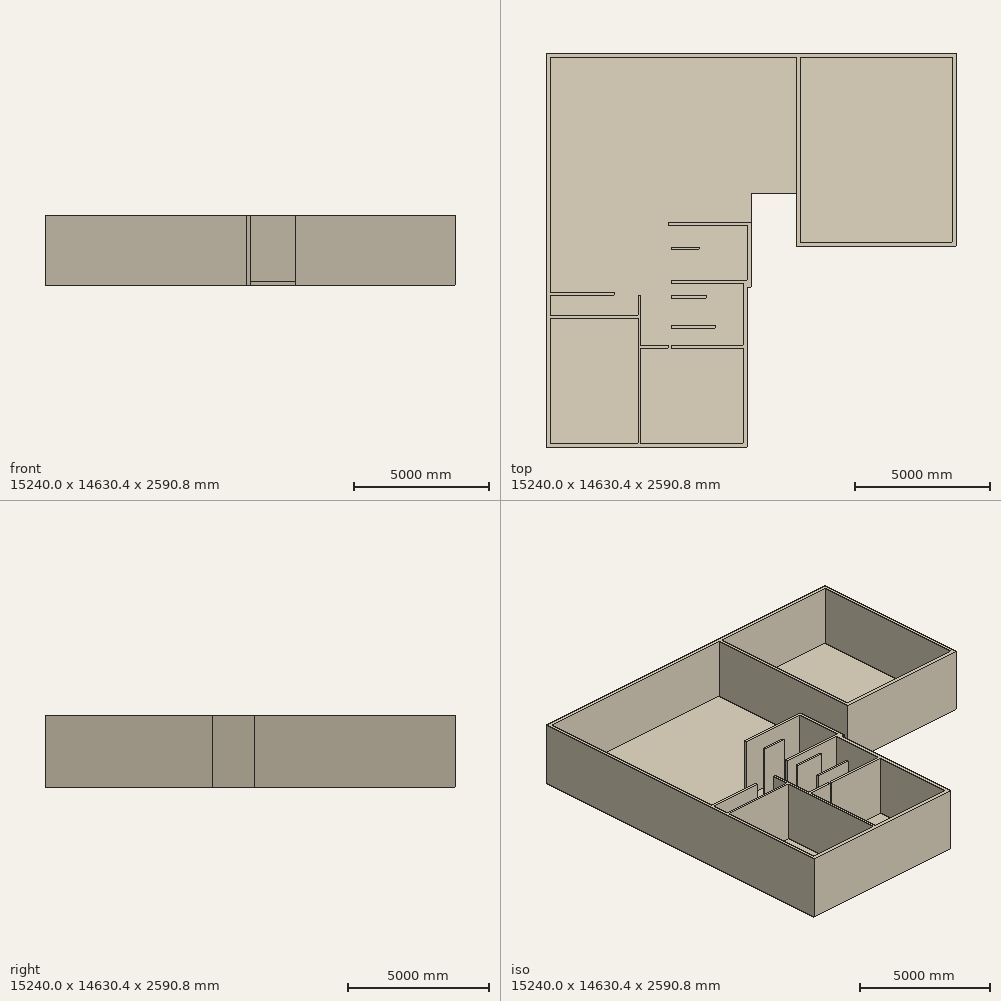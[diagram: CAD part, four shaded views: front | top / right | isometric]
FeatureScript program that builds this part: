
annotation { "Feature Type Name" : "Feature", "Feature Type Description" : "" }
export const myFeature = defineFeature(function(context is Context, id is Id, definition is map)
    precondition{}
    {
        {
            var Q0;
            Q0=qCreatedBy(makeId("Top.planeOp"),FACE);
            var sketch = newSketch(context, id + "F0", { "sketchPlane" : qUnion([Q0])});
            skLineSegment(sketch, "E0", {"start": v(0, 0) * mm, "end": v(0, -14630.4) * mm});
            skLineSegment(sketch, "E1", {"start": v(0, -14630.4) * mm, "end": v(7467.6, -14630.4) * mm});
            skLineSegment(sketch, "E2", {"start": v(7620, -8686.8) * mm, "end": v(7620, -5181.6) * mm});
            skLineSegment(sketch, "E3", {"start": v(7620, -5181.6) * mm, "end": v(9296.4, -5181.6) * mm});
            skLineSegment(sketch, "E4", {"start": v(9296.4, -5181.6) * mm, "end": v(9296.4, -7162.8) * mm});
            skLineSegment(sketch, "E5", {"start": v(9296.4, -7162.8) * mm, "end": v(15240, -7162.8) * mm});
            skLineSegment(sketch, "E6", {"start": v(15240, -7162.8) * mm, "end": v(15240, 0) * mm});
            skLineSegment(sketch, "E7", {"start": v(15240, 0) * mm, "end": v(0, 0) * mm});
            skLineSegment(sketch, "E8.0", {"start": v(15087.6, -152.4) * mm, "end": v(152.4, -152.4) * mm});
            skLineSegment(sketch, "E8.1", {"start": v(15087.6, -7010.4) * mm, "end": v(15087.6, -152.4) * mm});
            skLineSegment(sketch, "E8.2", {"start": v(9448.8, -7010.4) * mm, "end": v(15087.6, -7010.4) * mm});
            skLineSegment(sketch, "E8.3", {"start": v(9448.8, -5029.2) * mm, "end": v(9448.8, -7010.4) * mm});
            skLineSegment(sketch, "E8.4", {"start": v(7467.6, -5029.2) * mm, "end": v(9448.8, -5029.2) * mm});
            skLineSegment(sketch, "E8.5", {"start": v(152.4, -152.4) * mm, "end": v(152.4, -14478) * mm});
            skLineSegment(sketch, "E8.6", {"start": v(7467.6, -8534.4) * mm, "end": v(7467.6, -5029.2) * mm});
            skLineSegment(sketch, "E8.7", {"start": v(152.4, -14478) * mm, "end": v(7315.2, -14478) * mm});
            skLineSegment(sketch, "E9", {"start": v(7315.2, -14478) * mm, "end": v(7315.2, -8534.4) * mm});
            skLineSegment(sketch, "E10", {"start": v(7315.2, -8534.4) * mm, "end": v(7467.6, -8534.4) * mm});
            skLineSegment(sketch, "E11.0", {"start": v(7467.6, -8686.8) * mm, "end": v(7620, -8686.8) * mm});
            skLineSegment(sketch, "E11.1", {"start": v(7467.6, -14630.4) * mm, "end": v(7467.6, -8686.8) * mm});
            skSolve(sketch);
        }
        {
            var Q0;
            Q0=makeQuery(id+"F0.imprint","IMPRINT",FACE,{"disambiguationData":[TD([[makeQuery(id+"F0.imprint","IMPRINT",EDGE,{"derivedFrom":sQuery(id+"F0.wireOp",EDGE,"E0")}),1.0]])]});
            var Q1;
            Q1=makeQuery(id+"F0.imprint","IMPRINT",FACE,{"disambiguationData":[TD([[makeQuery(id+"F0.imprint","IMPRINT",EDGE,{"derivedFrom":sQuery(id+"F0.wireOp",EDGE,"E8.0")}),1.0]])]});
            extrude(context, id + "F1", {"entities" : qUnion([Q0, Q1]), "oppositeDirection" : true, "depth" : 152.4 * mm});
        }
        {
            var Q0;
            Q0=makeQuery(id+"F0.imprint","IMPRINT",FACE,{"disambiguationData":[TD([[makeQuery(id+"F0.imprint","IMPRINT",EDGE,{"derivedFrom":sQuery(id+"F0.wireOp",EDGE,"E0")}),1.0]])]});
            extrude(context, id + "F2", {"entities" : qUnion([Q0]), "depth" : 2438.4 * mm});
        }
        {
            var Q0;
            Q0=qCreatedBy(makeId("Top.planeOp"),FACE);
            var sketch = newSketch(context, id + "F3", { "sketchPlane" : qUnion([Q0])});
            skLineSegment(sketch, "E12.bottom", {"start": v(9448.8, -5029.2) * mm, "end": v(9296.4, -5029.2) * mm});
            skLineSegment(sketch, "E12.top", {"start": v(9448.8, -152.4) * mm, "end": v(9296.4, -152.4) * mm});
            skLineSegment(sketch, "E12.left", {"start": v(9448.8, -5029.2) * mm, "end": v(9448.8, -152.4) * mm});
            skLineSegment(sketch, "E12.right", {"start": v(9296.4, -5029.2) * mm, "end": v(9296.4, -152.4) * mm});
            skLineSegment(sketch, "E13.bottom", {"start": v(7467.6, -5029.2) * mm, "end": v(4546.6, -5029.2) * mm});
            skLineSegment(sketch, "E13.top", {"start": v(7467.6, -5130.8) * mm, "end": v(4546.6, -5130.8) * mm});
            skLineSegment(sketch, "E13.left", {"start": v(7467.6, -5029.2) * mm, "end": v(7467.6, -5130.8) * mm});
            skLineSegment(sketch, "E13.right", {"start": v(4546.6, -5029.2) * mm, "end": v(4546.6, -5130.8) * mm});
            skLineSegment(sketch, "E14.bottom", {"start": v(6096, -5029.2) * mm, "end": v(6197.6, -5029.2) * mm});
            skLineSegment(sketch, "E14.top", {"start": v(6096, -1625.6) * mm, "end": v(6197.6, -1625.6) * mm});
            skLineSegment(sketch, "E14.left", {"start": v(6096, -5029.2) * mm, "end": v(6096, -1625.6) * mm});
            skLineSegment(sketch, "E14.right", {"start": v(6197.6, -5029.2) * mm, "end": v(6197.6, -1625.6) * mm});
            skLineSegment(sketch, "E15.bottom", {"start": v(4546.6, -5029.2) * mm, "end": v(4648.2, -5029.2) * mm});
            skLineSegment(sketch, "E15.top", {"start": v(4546.6, -4191) * mm, "end": v(4648.2, -4191) * mm});
            skLineSegment(sketch, "E15.left", {"start": v(4546.6, -5029.2) * mm, "end": v(4546.6, -4191) * mm});
            skLineSegment(sketch, "E15.right", {"start": v(4648.2, -5029.2) * mm, "end": v(4648.2, -4191) * mm});
            skLineSegment(sketch, "E16.bottom", {"start": v(4648.2, -4191) * mm, "end": v(6096, -4191) * mm});
            skLineSegment(sketch, "E16.top", {"start": v(4648.2, -4292.6) * mm, "end": v(6096, -4292.6) * mm});
            skLineSegment(sketch, "E16.left", {"start": v(4648.2, -4191) * mm, "end": v(4648.2, -4292.6) * mm});
            skLineSegment(sketch, "E16.right", {"start": v(6096, -4191) * mm, "end": v(6096, -4292.6) * mm});
            skLineSegment(sketch, "E17.bottom", {"start": v(152.4, -4191) * mm, "end": v(3505.2, -4191) * mm});
            skLineSegment(sketch, "E17.top", {"start": v(152.4, -4292.6) * mm, "end": v(3505.2, -4292.6) * mm});
            skLineSegment(sketch, "E17.left", {"start": v(152.4, -4191) * mm, "end": v(152.4, -4292.6) * mm});
            skLineSegment(sketch, "E17.right", {"start": v(3505.2, -4191) * mm, "end": v(3505.2, -4292.6) * mm});
            skLineSegment(sketch, "E18.bottom", {"start": v(3505.2, -4292.6) * mm, "end": v(3403.6, -4292.6) * mm});
            skLineSegment(sketch, "E18.top", {"start": v(3505.2, -8991.6) * mm, "end": v(3403.6, -8991.6) * mm});
            skLineSegment(sketch, "E18.left", {"start": v(3505.2, -4292.6) * mm, "end": v(3505.2, -8991.6) * mm});
            skLineSegment(sketch, "E18.right", {"start": v(3403.6, -4292.6) * mm, "end": v(3403.6, -8991.6) * mm});
            skLineSegment(sketch, "E19.bottom", {"start": v(2540, -8991.6) * mm, "end": v(152.4, -8991.6) * mm});
            skLineSegment(sketch, "E19.top", {"start": v(2540, -8890) * mm, "end": v(152.4, -8890) * mm});
            skLineSegment(sketch, "E19.left", {"start": v(3403.6, -8991.6) * mm, "end": v(3403.6, -8890) * mm});
            skLineSegment(sketch, "E19.right", {"start": v(152.4, -8991.6) * mm, "end": v(152.4, -8890) * mm});
            skLineSegment(sketch, "E20.bottom", {"start": v(3403.6, -8051.8) * mm, "end": v(152.4, -8051.8) * mm});
            skLineSegment(sketch, "E20.top", {"start": v(3403.6, -8153.4) * mm, "end": v(152.4, -8153.4) * mm});
            skLineSegment(sketch, "E20.left", {"start": v(3403.6, -8051.8) * mm, "end": v(3403.6, -8153.4) * mm});
            skLineSegment(sketch, "E20.right", {"start": v(152.4, -8051.8) * mm, "end": v(152.4, -8153.4) * mm});
            skLineSegment(sketch, "E21.bottom", {"start": v(7467.6, -6375.4) * mm, "end": v(4546.6, -6375.4) * mm});
            skLineSegment(sketch, "E21.top", {"start": v(7467.6, -6273.8) * mm, "end": v(4546.6, -6273.8) * mm});
            skLineSegment(sketch, "E21.left", {"start": v(7467.6, -6375.4) * mm, "end": v(7467.6, -6273.8) * mm});
            skLineSegment(sketch, "E21.right", {"start": v(4546.6, -6375.4) * mm, "end": v(4546.6, -6273.8) * mm});
            skLineSegment(sketch, "E22.bottom", {"start": v(4546.6, -6375.4) * mm, "end": v(4648.2, -6375.4) * mm});
            skLineSegment(sketch, "E22.top", {"start": v(4546.6, -10947.4) * mm, "end": v(4648.2, -10947.4) * mm});
            skLineSegment(sketch, "E22.left", {"start": v(4546.6, -6375.4) * mm, "end": v(4546.6, -10947.4) * mm});
            skLineSegment(sketch, "E22.right", {"start": v(4648.2, -6375.4) * mm, "end": v(4648.2, -10947.4) * mm});
            skLineSegment(sketch, "E23.bottom", {"start": v(4648.2, -8432.8) * mm, "end": v(7467.6, -8432.8) * mm});
            skLineSegment(sketch, "E23.top", {"start": v(4648.2, -8534.4) * mm, "end": v(7467.6, -8534.4) * mm});
            skLineSegment(sketch, "E23.left", {"start": v(4648.2, -8432.8) * mm, "end": v(4648.2, -8534.4) * mm});
            skLineSegment(sketch, "E23.right", {"start": v(7467.6, -8432.8) * mm, "end": v(7467.6, -8534.4) * mm});
            skLineSegment(sketch, "E24.bottom", {"start": v(4648.2, -10947.4) * mm, "end": v(7315.2, -10947.4) * mm});
            skLineSegment(sketch, "E24.top", {"start": v(4648.2, -10845.8) * mm, "end": v(7315.2, -10845.8) * mm});
            skLineSegment(sketch, "E24.left", {"start": v(4648.2, -10947.4) * mm, "end": v(4648.2, -10845.8) * mm});
            skLineSegment(sketch, "E24.right", {"start": v(7315.2, -10947.4) * mm, "end": v(7315.2, -10845.8) * mm});
            skLineSegment(sketch, "E25.top", {"start": v(3505.2, -14478) * mm, "end": v(3403.6, -14478) * mm});
            skLineSegment(sketch, "E25.left", {"start": v(3505.2, -8991.6) * mm, "end": v(3505.2, -14478) * mm});
            skLineSegment(sketch, "E25.right", {"start": v(3403.6, -8991.6) * mm, "end": v(3403.6, -14478) * mm});
            skLineSegment(sketch, "E26.bottom", {"start": v(3403.6, -9829.8) * mm, "end": v(152.4, -9829.8) * mm});
            skLineSegment(sketch, "E26.top", {"start": v(3403.6, -9728.2) * mm, "end": v(152.4, -9728.2) * mm});
            skLineSegment(sketch, "E26.left", {"start": v(3403.6, -9829.8) * mm, "end": v(3403.6, -9728.2) * mm});
            skLineSegment(sketch, "E26.right", {"start": v(152.4, -9829.8) * mm, "end": v(152.4, -9728.2) * mm});
            skLineSegment(sketch, "E27.bottom", {"start": v(4546.6, -10947.4) * mm, "end": v(3505.2, -10947.4) * mm});
            skLineSegment(sketch, "E27.top", {"start": v(4546.6, -10845.8) * mm, "end": v(3505.2, -10845.8) * mm});
            skLineSegment(sketch, "E27.left", {"start": v(4546.6, -10947.4) * mm, "end": v(4546.6, -10845.8) * mm});
            skLineSegment(sketch, "E27.right", {"start": v(3505.2, -10947.4) * mm, "end": v(3505.2, -10845.8) * mm});
            skLineSegment(sketch, "E28.bottom", {"start": v(4648.2, -10210.8) * mm, "end": v(6273.8, -10210.8) * mm});
            skLineSegment(sketch, "E28.top", {"start": v(4648.2, -10109.2) * mm, "end": v(6273.8, -10109.2) * mm});
            skLineSegment(sketch, "E28.left", {"start": v(4648.2, -10210.8) * mm, "end": v(4648.2, -10109.2) * mm});
            skLineSegment(sketch, "E28.right", {"start": v(6273.8, -10210.8) * mm, "end": v(6273.8, -10109.2) * mm});
            skLineSegment(sketch, "E29.bottom", {"start": v(6273.8, -10210.8) * mm, "end": v(6172.2, -10210.8) * mm});
            skLineSegment(sketch, "E29.top", {"start": v(6273.8, -10845.8) * mm, "end": v(6172.2, -10845.8) * mm});
            skLineSegment(sketch, "E29.left", {"start": v(6273.8, -10210.8) * mm, "end": v(6273.8, -10845.8) * mm});
            skLineSegment(sketch, "E29.right", {"start": v(6172.2, -10210.8) * mm, "end": v(6172.2, -10845.8) * mm});
            skLineSegment(sketch, "E30.bottom", {"start": v(2540, -8153.4) * mm, "end": v(2641.6, -8153.4) * mm});
            skLineSegment(sketch, "E30.top", {"start": v(2540, -9728.2) * mm, "end": v(2641.6, -9728.2) * mm});
            skLineSegment(sketch, "E30.left", {"start": v(2540, -8153.4) * mm, "end": v(2540, -9728.2) * mm});
            skLineSegment(sketch, "E30.right", {"start": v(2641.6, -8153.4) * mm, "end": v(2641.6, -9728.2) * mm});
            skLineSegment(sketch, "E31.bottom", {"start": v(4648.2, -7289.8) * mm, "end": v(5689.6, -7289.8) * mm});
            skLineSegment(sketch, "E31.top", {"start": v(4648.2, -7188.2) * mm, "end": v(5689.6, -7188.2) * mm});
            skLineSegment(sketch, "E31.left", {"start": v(4648.2, -7289.8) * mm, "end": v(4648.2, -7188.2) * mm});
            skLineSegment(sketch, "E31.right", {"start": v(5689.6, -7289.8) * mm, "end": v(5689.6, -7188.2) * mm});
            skLineSegment(sketch, "E32.bottom", {"start": v(5689.6, -7188.2) * mm, "end": v(5588, -7188.2) * mm});
            skLineSegment(sketch, "E32.top", {"start": v(5689.6, -6375.4) * mm, "end": v(5588, -6375.4) * mm});
            skLineSegment(sketch, "E32.left", {"start": v(5689.6, -7188.2) * mm, "end": v(5689.6, -6375.4) * mm});
            skLineSegment(sketch, "E32.right", {"start": v(5588, -7188.2) * mm, "end": v(5588, -6375.4) * mm});
            skLineSegment(sketch, "E33.bottom", {"start": v(4648.2, -8991.6) * mm, "end": v(5943.6, -8991.6) * mm});
            skLineSegment(sketch, "E33.top", {"start": v(4648.2, -9093.2) * mm, "end": v(5943.6, -9093.2) * mm});
            skLineSegment(sketch, "E33.left", {"start": v(4648.2, -8991.6) * mm, "end": v(4648.2, -9093.2) * mm});
            skLineSegment(sketch, "E33.right", {"start": v(5943.6, -8991.6) * mm, "end": v(5943.6, -9093.2) * mm});
            skLineSegment(sketch, "E34.bottom", {"start": v(5943.6, -8991.6) * mm, "end": v(5842, -8991.6) * mm});
            skLineSegment(sketch, "E34.top", {"start": v(5943.6, -8534.4) * mm, "end": v(5842, -8534.4) * mm});
            skLineSegment(sketch, "E34.left", {"start": v(5943.6, -8991.6) * mm, "end": v(5943.6, -8534.4) * mm});
            skLineSegment(sketch, "E34.right", {"start": v(5842, -8991.6) * mm, "end": v(5842, -8534.4) * mm});
            skSolve(sketch);
        }
        {
            var Q0;
            Q0=makeQuery(id+"F3.imprint","IMPRINT",FACE,{"disambiguationData":[TD([[makeQuery(id+"F3.imprint","IMPRINT",EDGE,{"derivedFrom":sQuery(id+"F3.wireOp",EDGE,"E12.bottom")}),-1.0]])]});
            var Q1;
            Q1=makeQuery(id+"F3.imprint","IMPRINT",FACE,{"disambiguationData":[TD([[makeQuery(id+"F3.imprint","IMPRINT",EDGE,{"derivedFrom":sQuery(id+"F3.wireOp",EDGE,"E13.top")}),-1.0]])]});
            var Q2;
            Q2=makeQuery(id+"F3.imprint","IMPRINT",FACE,{"disambiguationData":[TD([[makeQuery(id+"F3.imprint","IMPRINT",EDGE,{"derivedFrom":sQuery(id+"F3.wireOp",EDGE,"E15.bottom")}),1.0]])]});
            var Q3;
            Q3=makeQuery(id+"F3.imprint","IMPRINT",FACE,{"disambiguationData":[TD([[makeQuery(id+"F3.imprint","IMPRINT",EDGE,{"derivedFrom":sQuery(id+"F3.wireOp",EDGE,"E16.bottom")}),-1.0]])]});
            var Q4;
            {var subQ3=sQuery(id+"F3.wireOp",EDGE,"E14.bottom");Q4=makeQuery(id+"F3.imprint","IMPRINT",FACE,{"disambiguationData":[TD([[makeQuery(id+"F3.imprint","IMPRINT",EDGE,{"derivedFrom":subQ3}),1.0]])]});}
            var Q5;
            Q5=makeQuery(id+"F3.imprint","IMPRINT",FACE,{"disambiguationData":[TD([[makeQuery(id+"F3.imprint","IMPRINT",EDGE,{"derivedFrom":sQuery(id+"F3.wireOp",EDGE,"E17.bottom")}),-1.0]])]});
            var Q6;
            {var subQ3=sQuery(id+"F3.wireOp",EDGE,"E18.bottom");Q6=makeQuery(id+"F3.imprint","IMPRINT",FACE,{"disambiguationData":[TD([[makeQuery(id+"F3.imprint","IMPRINT",EDGE,{"derivedFrom":subQ3}),1.0]])]});}
            var Q7;
            Q7=makeQuery(id+"F3.imprint","IMPRINT",FACE,{"disambiguationData":[TD([[makeQuery(id+"F3.imprint","IMPRINT",EDGE,{"derivedFrom":sQuery(id+"F3.wireOp",EDGE,"E21.bottom")}),-1.0]])]});
            var Q8;
            {var subQ4=sQuery(id+"F3.wireOp",EDGE,"E22.bottom");Q8=makeQuery(id+"F3.imprint","IMPRINT",FACE,{"disambiguationData":[TD([[makeQuery(id+"F3.imprint","IMPRINT",EDGE,{"derivedFrom":subQ4}),-1.0]])]});}
            var Q9;
            Q9=makeQuery(id+"F3.imprint","IMPRINT",FACE,{"disambiguationData":[TD([[makeQuery(id+"F3.imprint","IMPRINT",EDGE,{"derivedFrom":sQuery(id+"F3.wireOp",EDGE,"E23.bottom")}),-1.0]])]});
            var Q10;
            Q10=makeQuery(id+"F3.imprint","IMPRINT",FACE,{"disambiguationData":[TD([[makeQuery(id+"F3.imprint","IMPRINT",EDGE,{"derivedFrom":sQuery(id+"F3.wireOp",EDGE,"E28.bottom")}),1.0]])]});
            var Q11;
            Q11=makeQuery(id+"F3.imprint","IMPRINT",FACE,{"disambiguationData":[TD([[makeQuery(id+"F3.imprint","IMPRINT",EDGE,{"derivedFrom":sQuery(id+"F3.wireOp",EDGE,"E29.bottom")}),1.0]])]});
            var Q12;
            Q12=makeQuery(id+"F3.imprint","IMPRINT",FACE,{"disambiguationData":[TD([[makeQuery(id+"F3.imprint","IMPRINT",EDGE,{"derivedFrom":sQuery(id+"F3.wireOp",EDGE,"E24.bottom")}),1.0]])]});
            var Q13;
            Q13=makeQuery(id+"F3.imprint","IMPRINT",FACE,{"disambiguationData":[TD([[makeQuery(id+"F3.imprint","IMPRINT",EDGE,{"derivedFrom":sQuery(id+"F3.wireOp",EDGE,"E20.bottom")}),1.0]])]});
            var Q14;
            Q14=makeQuery(id+"F3.imprint","IMPRINT",FACE,{"disambiguationData":[TD([[makeQuery(id+"F3.imprint","IMPRINT",EDGE,{"derivedFrom":sQuery(id+"F3.wireOp",EDGE,"E19.bottom")}),-1.0]])]});
            var Q15;
            Q15=makeQuery(id+"F3.imprint","IMPRINT",FACE,{"disambiguationData":[TD([[makeQuery(id+"F3.imprint","IMPRINT",EDGE,{"derivedFrom":sQuery(id+"F3.wireOp",EDGE,"E26.bottom")}),-1.0]])]});
            var Q16;
            {var subQ4=sQuery(id+"F3.wireOp",EDGE,"E18.top");Q16=makeQuery(id+"F3.imprint","IMPRINT",FACE,{"disambiguationData":[TD([[makeQuery(id+"F3.imprint","IMPRINT",EDGE,{"derivedFrom":subQ4}),1.0]])]});}
            var Q17;
            Q17=makeQuery(id+"F3.imprint","IMPRINT",FACE,{"disambiguationData":[TD([[makeQuery(id+"F3.imprint","IMPRINT",EDGE,{"derivedFrom":sQuery(id+"F3.wireOp",EDGE,"E27.bottom")}),-1.0]])]});
            var Q18;
            {var subQ4=sQuery(id+"F3.wireOp",EDGE,"E30.bottom");Q18=makeQuery(id+"F3.imprint","IMPRINT",FACE,{"disambiguationData":[TD([[makeQuery(id+"F3.imprint","IMPRINT",EDGE,{"derivedFrom":subQ4}),-1.0]])]});}
            var Q19;
            Q19=makeQuery(id+"F3.imprint","IMPRINT",FACE,{"disambiguationData":[TD([[makeQuery(id+"F3.imprint","IMPRINT",EDGE,{"derivedFrom":sQuery(id+"F3.wireOp",EDGE,"E31.bottom")}),1.0]])]});
            var Q20;
            Q20=makeQuery(id+"F3.imprint","IMPRINT",FACE,{"disambiguationData":[TD([[makeQuery(id+"F3.imprint","IMPRINT",EDGE,{"derivedFrom":sQuery(id+"F3.wireOp",EDGE,"E32.bottom")}),-1.0]])]});
            var Q21;
            Q21=makeQuery(id+"F3.imprint","IMPRINT",FACE,{"disambiguationData":[TD([[makeQuery(id+"F3.imprint","IMPRINT",EDGE,{"derivedFrom":sQuery(id+"F3.wireOp",EDGE,"E33.bottom")}),-1.0]])]});
            var Q22;
            Q22=makeQuery(id+"F3.imprint","IMPRINT",FACE,{"disambiguationData":[TD([[makeQuery(id+"F3.imprint","IMPRINT",EDGE,{"derivedFrom":sQuery(id+"F3.wireOp",EDGE,"E34.bottom")}),-1.0]])]});
            var Q23;
            Q23=makeQuery(id+"F2.opExtrude","CAP_FACE",FACE,{"disambiguationData":[OSD([sQuery(id+"F0.wireOp",EDGE,"E0"),sQuery(id+"F0.wireOp",EDGE,"E1"),sQuery(id+"F0.wireOp",EDGE,"E2"),sQuery(id+"F0.wireOp",EDGE,"E3"),sQuery(id+"F0.wireOp",EDGE,"E4"),sQuery(id+"F0.wireOp",EDGE,"E5"),sQuery(id+"F0.wireOp",EDGE,"E6"),sQuery(id+"F0.wireOp",EDGE,"E7"),sQuery(id+"F0.wireOp",EDGE,"E8.0"),sQuery(id+"F0.wireOp",EDGE,"E8.1"),sQuery(id+"F0.wireOp",EDGE,"E8.2"),sQuery(id+"F0.wireOp",EDGE,"E8.3"),sQuery(id+"F0.wireOp",EDGE,"E8.4"),sQuery(id+"F0.wireOp",EDGE,"E8.5"),sQuery(id+"F0.wireOp",EDGE,"E8.6"),sQuery(id+"F0.wireOp",EDGE,"E8.7"),sQuery(id+"F0.wireOp",EDGE,"E9"),sQuery(id+"F0.wireOp",EDGE,"E10"),sQuery(id+"F0.wireOp",EDGE,"E11.0"),sQuery(id+"F0.wireOp",EDGE,"E11.1")])],"isStart":false});
            extrude(context, id + "F4", {"entities" : qUnion([Q0, Q1, Q2, Q3, Q4, Q5, Q6, Q7, Q8, Q9, Q10, Q11, Q12, Q13, Q14, Q15, Q16, Q17, Q18, Q19, Q20, Q21, Q22]), "operationType" : NewBodyOperationType.ADD, "endBound" : BoundingType.UP_TO_SURFACE, "endBoundEntityFace" : qUnion([Q23]), "depth" : 1488.9 * mm});
        }
        {
            var Q0;
            Q0=qCreatedBy(makeId("Top.planeOp"),FACE);
            var sketch = newSketch(context, id + "F5", { "sketchPlane" : qUnion([Q0])});
            skPoint(sketch, "E35.orphan", {"position": v(7467.6, -8534.4) * mm});
            skLineSegment(sketch, "E36.bottom", {"start": v(4108.86, -1470.97) * mm, "end": v(9296.4, -1470.97) * mm});
            skLineSegment(sketch, "E36.top", {"start": v(4108.86, -6273.8) * mm, "end": v(9296.4, -6273.8) * mm});
            skLineSegment(sketch, "E36.left", {"start": v(4108.86, -1470.97) * mm, "end": v(4108.86, -6273.8) * mm});
            skLineSegment(sketch, "E36.right", {"start": v(9296.4, -1470.97) * mm, "end": v(9296.4, -6273.8) * mm});
            skSolve(sketch);
        }
        {
            var Q0;
            Q0 = qSketchRegion(id + "F5", true);
            extrude(context, id + "F6", {"entities" : qUnion([Q0]), "operationType" : NewBodyOperationType.REMOVE, "endBound" : BoundingType.THROUGH_ALL, "depth" : 25.4 * mm});
        }
        {
            var Q0;
            Q0=qCreatedBy(makeId("Top.planeOp"),FACE);
            var sketch = newSketch(context, id + "F7", { "sketchPlane" : qUnion([Q0])});
            skLineSegment(sketch, "E37.bottom", {"start": v(3939.4, -3772.57) * mm, "end": v(152.4, -3772.57) * mm});
            skLineSegment(sketch, "E37.top", {"start": v(3939.4, -8890) * mm, "end": v(152.4, -8890) * mm});
            skLineSegment(sketch, "E37.left", {"start": v(3939.4, -3772.57) * mm, "end": v(3939.4, -8890) * mm});
            skLineSegment(sketch, "E37.right", {"start": v(152.4, -3772.57) * mm, "end": v(152.4, -8890) * mm});
            skSolve(sketch);
        }
        {
            var Q0;
            Q0=makeQuery(id+"F7.imprint","IMPRINT",FACE,{"disambiguationData":[TD([[makeQuery(id+"F7.imprint","IMPRINT",EDGE,{"derivedFrom":sQuery(id+"F7.wireOp",EDGE,"E37.bottom")}),1.0]])]});
            extrude(context, id + "F8", {"entities" : qUnion([Q0]), "operationType" : NewBodyOperationType.REMOVE, "endBound" : BoundingType.THROUGH_ALL, "depth" : 25.4 * mm});
        }
    });
